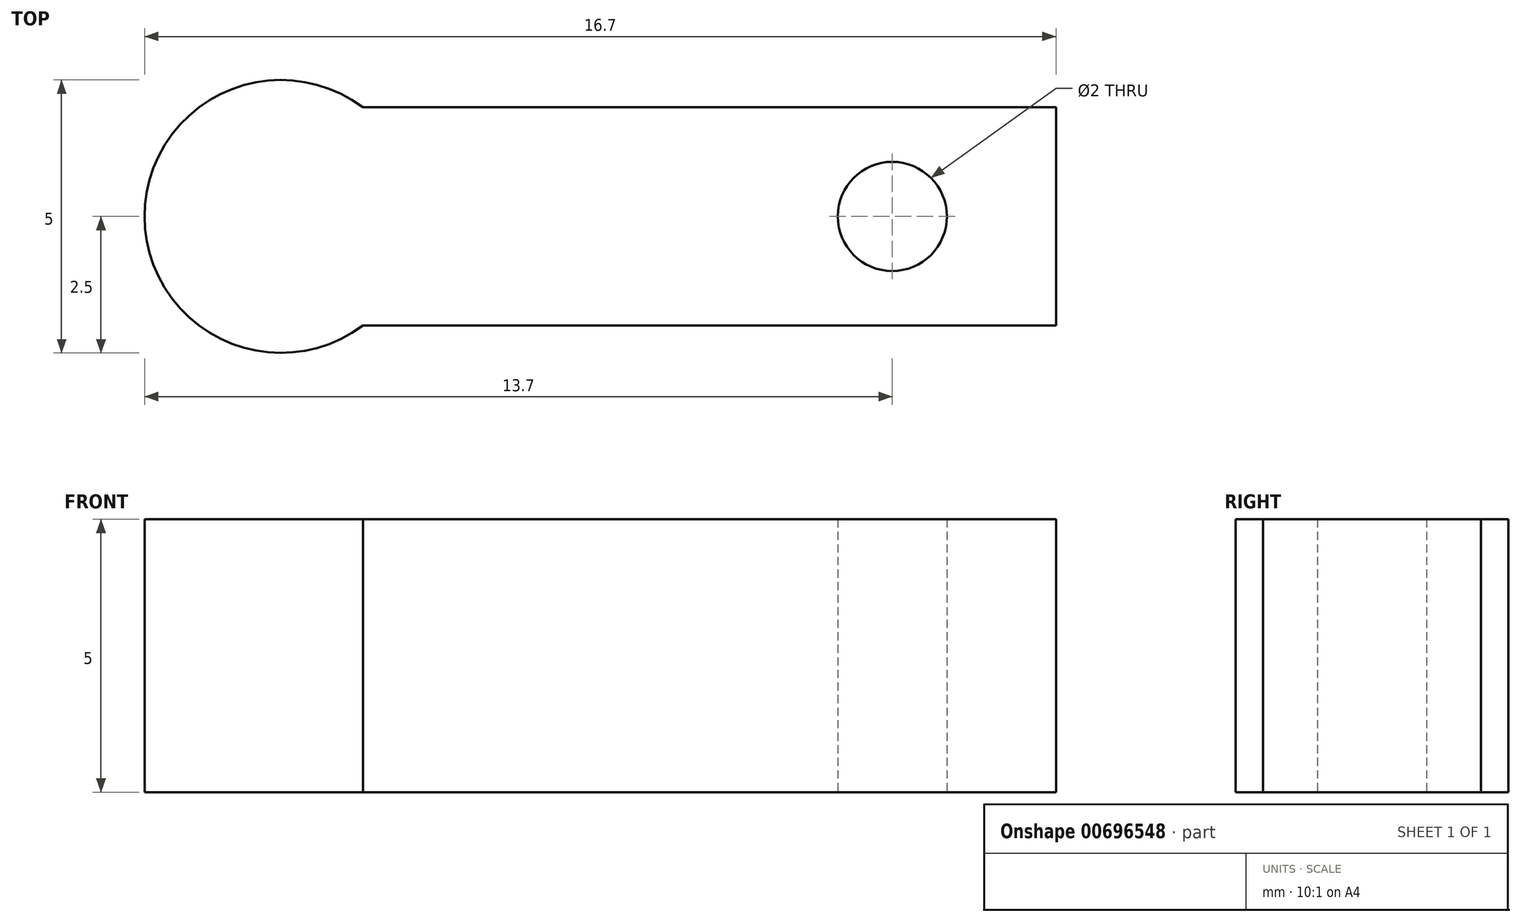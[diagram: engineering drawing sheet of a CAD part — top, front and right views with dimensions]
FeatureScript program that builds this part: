
annotation { "Feature Type Name" : "Feature", "Feature Type Description" : "" }
export const myFeature = defineFeature(function(context is Context, id is Id, definition is map)
    precondition{}
    {
        {
            var Q0;
            Q0=qCreatedBy(makeId("Top.planeOp"),FACE);
            var sketch = newSketch(context, id + "F0", { "sketchPlane" : qUnion([Q0])});
            skArc(sketch, "E0", {"start": v(1.5, 2) * mm, "mid": v(-2.5, 0) * mm, "end": v(1.5, -2) * mm});
            skLineSegment(sketch, "E1", {"start": v(1.5, 2) * mm, "end": v(14.2, 2) * mm});
            skLineSegment(sketch, "E2", {"start": v(14.2, 2) * mm, "end": v(14.2, -2) * mm});
            skLineSegment(sketch, "E3", {"start": v(14.2, -2) * mm, "end": v(1.5, -2) * mm});
            skPoint(sketch, "E4", {"position": v(14.2, 0) * mm});
            skCircle(sketch, "E5", {"center": v(11.2, 0) * mm, "radius": 1 * mm});
            skSolve(sketch);
        }
        {
            var Q0;
            Q0 = qSketchRegion(id + "F0", true);
            extrude(context, id + "F1", {"entities" : qUnion([Q0]), "depth" : 5 * mm, "offsetDistance" : 25.4 * mm});
        }
    });
